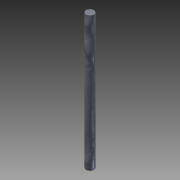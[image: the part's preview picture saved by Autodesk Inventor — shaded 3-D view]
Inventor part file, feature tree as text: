
AUTODESK INVENTOR PART (.ipt)
format: ipt  version: 2015 (Build 190159000, 159)  size: 91,648 bytes
history: native  units: mm
features: other x1, extrude x1, sketch x1
ambient origin geometry x8: Origin, YZ Plane, XZ Plane, XY Plane, X Axis, Y Axis, Z Axis, Center Point
bodies: Body1 (feature_tree)
feature tree (3):
  other  "ソリッド1"
  extrude  "押し出し1"  Depth=3.0mm
  sketch  "スケッチ1"
